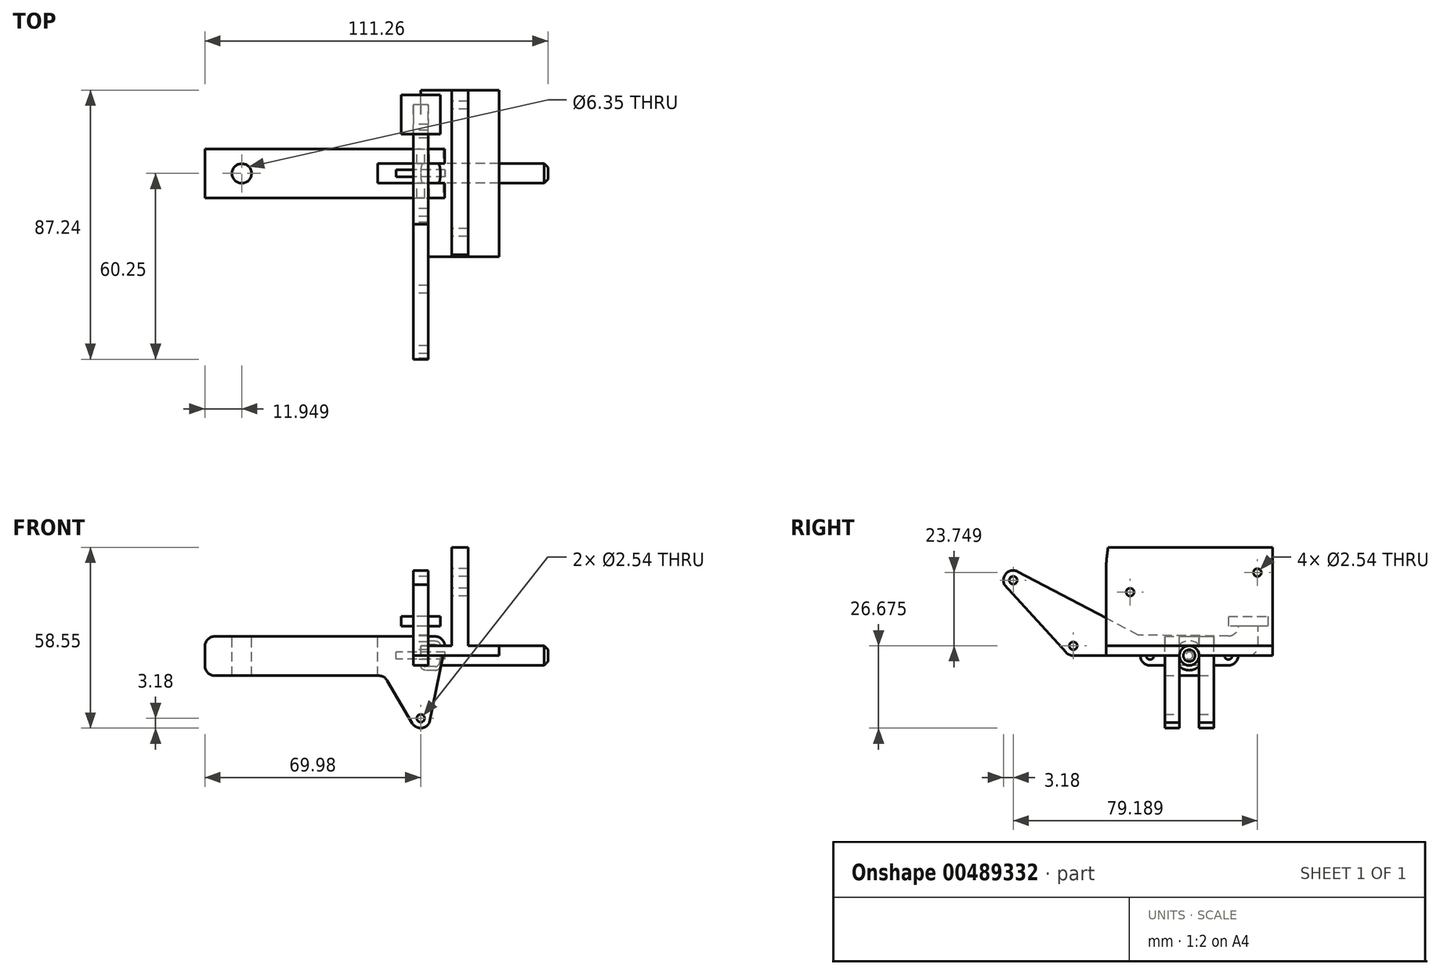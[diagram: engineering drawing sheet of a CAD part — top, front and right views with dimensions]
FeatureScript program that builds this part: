
annotation { "Feature Type Name" : "Feature", "Feature Type Description" : "" }
export const myFeature = defineFeature(function(context is Context, id is Id, definition is map)
    precondition{}
    {
        {
            var Q0;
            Q0=qCreatedBy(makeId("Front.planeOp"),FACE);
            var sketch = newSketch(context, id + "F0", { "sketchPlane" : qUnion([Q0])});
            skCircle(sketch, "E0", {"center": v(0, 0) * mm, "radius": 1.27 * mm});
            skLineSegment(sketch, "E1", {"start": v(-24.73, 6.19) * mm, "end": v(4.64, 6.19) * mm});
            skLineSegment(sketch, "E2", {"start": v(7.75, 2.38) * mm, "end": v(2.83, -21.75) * mm});
            skLineSegment(sketch, "E3", {"start": v(-2.74, -21.93) * mm, "end": v(-10.89, -8.08) * mm});
            skLineSegment(sketch, "E4", {"start": v(-13.62, -6.51) * mm, "end": v(-66.8, -6.51) * mm});
            skLineSegment(sketch, "E5", {"start": v(-69.98, -3.34) * mm, "end": v(-69.98, 3.01) * mm});
            skLineSegment(sketch, "E6", {"start": v(-66.8, 6.19) * mm, "end": v(-24.73, 6.19) * mm});
            skPoint(sketch, "E7.visualSharp", {"position": v(8.53, 6.19) * mm});
            skArc(sketch, "E7.filletArc", {"start": v(7.75, 2.38) * mm, "mid": v(7.1, 5.02) * mm, "end": v(4.64, 6.19) * mm});
            skPoint(sketch, "E8.visualSharp", {"position": v(-11.8, -6.51) * mm});
            skArc(sketch, "E8.filletArc", {"start": v(-10.89, -8.08) * mm, "mid": v(-12.05, -6.93) * mm, "end": v(-13.62, -6.51) * mm});
            skPoint(sketch, "E9.visualSharp", {"position": v(-69.98, 6.19) * mm});
            skArc(sketch, "E9.filletArc", {"start": v(-66.8, 6.19) * mm, "mid": v(-69.05, 5.26) * mm, "end": v(-69.98, 3.01) * mm});
            skPoint(sketch, "E10.visualSharp", {"position": v(-69.98, -6.51) * mm});
            skArc(sketch, "E10.filletArc", {"start": v(-69.98, -3.34) * mm, "mid": v(-69.05, -5.58) * mm, "end": v(-66.8, -6.51) * mm});
            skArc(sketch, "E11", {"start": v(-2.74, -21.93) * mm, "mid": v(0.1, -23.5) * mm, "end": v(2.83, -21.75) * mm});
            skLineSegment(sketch, "E12", {"start": v(0, 0) * mm, "end": v(-69.98, -0.16) * mm, "construction": true});
            skCircle(sketch, "E13", {"center": v(0, -20.32) * mm, "radius": 1.27 * mm});
            skLineSegment(sketch, "E14", {"start": v(0, 0) * mm, "end": v(0, -20.32) * mm, "construction": true});
            skSolve(sketch);
        }
        {
            var Q0;
            Q0 = qSketchRegion(id + "F0", true);
            extrude(context, id + "F1", {"entities" : qUnion([Q0]), "endBound" : BoundingType.SYMMETRIC, "depth" : 15.88 * mm, "offsetDistance" : 25.4 * mm});
        }
        {
            var Q0;
            Q0=makeQuery(id+"F1.opExtrude","SWEPT_FACE",FACE,{"disambiguationData":[OSD([sQuery(id+"F0.wireOp",EDGE,"E1"),sQuery(id+"F0.wireOp",EDGE,"E6")])]});
            var sketch = newSketch(context, id + "F2", { "sketchPlane" : qUnion([Q0])});
            skLineSegment(sketch, "E15.0", {"start": v(7.75, -7.94) * mm, "end": v(7.75, 7.94) * mm});
            skLineSegment(sketch, "E16", {"start": v(7.75, 3.18) * mm, "end": v(-13.88, 3.18) * mm});
            skLineSegment(sketch, "E17", {"start": v(-13.88, 3.18) * mm, "end": v(-13.88, -3.17) * mm});
            skLineSegment(sketch, "E18", {"start": v(-13.88, -3.17) * mm, "end": v(7.75, -3.17) * mm});
            skLineSegment(sketch, "E19", {"start": v(7.75, 0) * mm, "end": v(-66.8, 0) * mm, "construction": true});
            skCircle(sketch, "E20", {"center": v(-58.03, 0) * mm, "radius": 3.18 * mm});
            skLineSegment(sketch, "E21.0", {"start": v(-66.8, 7.94) * mm, "end": v(4.64, 7.94) * mm});
            skLineSegment(sketch, "E22.0", {"start": v(-66.8, -7.94) * mm, "end": v(4.64, -7.94) * mm});
            skSolve(sketch);
        }
        {
            var Q0;
            Q0 = qSketchRegion(id + "F2", true);
            extrude(context, id + "F3", {"entities" : qUnion([Q0]), "operationType" : NewBodyOperationType.REMOVE, "endBound" : BoundingType.THROUGH_ALL, "oppositeDirection" : true, "depth" : 25.4 * mm, "offsetDistance" : 25.4 * mm});
        }
        {
            var Q0;
            {var subQ2=sQuery(id+"F0.wireOp",EDGE,"E2");Q0=makeQuery(id+"F3.boolean.opBoolean","SPLIT",FACE,{"disambiguationData":[TD([makeQuery(id+"F3.opExtrude","SWEPT_FACE",FACE,{"disambiguationData":[OSD([sQuery(id+"F2.wireOp",EDGE,"E16")])]})])],"derivedFrom":makeQuery(id+"F1.opExtrude","SWEPT_FACE",FACE,{"disambiguationData":[OSD([subQ2])]})});}
            var sketch = newSketch(context, id + "F4", { "sketchPlane" : qUnion([Q0])});
            skLineSegment(sketch, "E23.0", {"start": v(-3.17, 3.88) * mm, "end": v(3.18, 3.88) * mm});
            skLineSegment(sketch, "E24.0", {"start": v(3.18, 5.12) * mm, "end": v(-3.17, 5.12) * mm});
            skLineSegment(sketch, "E25", {"start": v(3.18, 5.12) * mm, "end": v(3.18, 3.88) * mm});
            skLineSegment(sketch, "E26", {"start": v(-3.17, 5.12) * mm, "end": v(-3.17, 3.88) * mm});
            skSolve(sketch);
        }
        {
            var Q0;
            Q0 = qSketchRegion(id + "F4", true);
            extrude(context, id + "F5", {"entities" : qUnion([Q0]), "operationType" : NewBodyOperationType.REMOVE, "oppositeDirection" : true, "depth" : 7.85 * mm, "offsetDistance" : 25.4 * mm});
        }
        {
            var Q0;
            Q0=qCreatedBy(makeId("Front.planeOp"),FACE);
            var sketch = newSketch(context, id + "F6", { "sketchPlane" : qUnion([Q0])});
            skLineSegment(sketch, "E27", {"start": v(0, 0) * mm, "end": v(25.4, 0) * mm});
            skLineSegment(sketch, "E28", {"start": v(0, 0) * mm, "end": v(0, 3.18) * mm});
            skLineSegment(sketch, "E29", {"start": v(0, 3.18) * mm, "end": v(15.36, 3.18) * mm});
            skLineSegment(sketch, "E30", {"start": v(25.4, 0) * mm, "end": v(25.4, 3.18) * mm});
            skLineSegment(sketch, "E31", {"start": v(25.4, 3.18) * mm, "end": v(10.04, 3.18) * mm});
            skLineSegment(sketch, "E32", {"start": v(15.36, 3.18) * mm, "end": v(15.36, 35.05) * mm});
            skLineSegment(sketch, "E33", {"start": v(10.04, 35.05) * mm, "end": v(15.36, 35.05) * mm});
            skLineSegment(sketch, "E34", {"start": v(10.04, 35.05) * mm, "end": v(10.04, 3.18) * mm});
            skSolve(sketch);
        }
        {
            var Q0;
            Q0 = qSketchRegion(id + "F6", true);
            extrude(context, id + "F7", {"entities" : qUnion([Q0]), "endBound" : BoundingType.SYMMETRIC, "depth" : 53.97 * mm, "offsetDistance" : 25.4 * mm});
        }
        {
            var Q0;
            Q0=makeQuery(id+"F7.opExtrude","SWEPT_FACE",FACE,{"disambiguationData":[OSD([sQuery(id+"F6.wireOp",EDGE,"E34")])]});
            var sketch = newSketch(context, id + "F8", { "sketchPlane" : qUnion([Q0])});
            skLineSegment(sketch, "E35.0.0", {"start": v(-26.99, 13.43) * mm, "end": v(-26.99, 3.18) * mm});
            skLineSegment(sketch, "E35.0.2", {"start": v(26.99, 3.18) * mm, "end": v(26.99, 26.92) * mm});
            skLineSegment(sketch, "E35.0.3", {"start": v(-26.99, 3.18) * mm, "end": v(26.99, 3.18) * mm});
            skPoint(sketch, "E36.visualSharp", {"position": v(26.99, 35.05) * mm});
            skLineSegment(sketch, "E37.0.0", {"start": v(-26.99, 0) * mm, "end": v(-26.99, 3.17) * mm});
            skLineSegment(sketch, "E37.0.1", {"start": v(-26.99, 3.17) * mm, "end": v(26.99, 3.17) * mm});
            skLineSegment(sketch, "E37.0.2", {"start": v(26.99, 3.17) * mm, "end": v(26.99, 0) * mm});
            skLineSegment(sketch, "E37.0.3", {"start": v(26.99, 0) * mm, "end": v(-26.99, 0) * mm});
            skArc(sketch, "E38", {"start": v(-71.23, 26.92) * mm, "mid": v(-22.12, 76.03) * mm, "end": v(26.99, 26.92) * mm});
            skCircle(sketch, "E39", {"center": v(-22.12, 26.92) * mm, "radius": 1.27 * mm});
            skLineSegment(sketch, "E40", {"start": v(-65.76, 17.46) * mm, "end": v(-71.23, 26.92) * mm});
            skLineSegment(sketch, "E41", {"start": v(-68.51, 12.7) * mm, "end": v(9.87, 12.7) * mm});
            skPoint(sketch, "E42.visualSharp", {"position": v(-63.01, 12.7) * mm});
            skArc(sketch, "E42.filletArc", {"start": v(-65.76, 17.46) * mm, "mid": v(-71.26, 17.46) * mm, "end": v(-68.51, 12.7) * mm});
            skPoint(sketch, "E43.visualSharp", {"position": v(12.82, 12.7) * mm});
            skArc(sketch, "E43.filletArc", {"start": v(9.87, 12.7) * mm, "mid": v(12.03, 13.55) * mm, "end": v(13.04, 15.65) * mm});
            skCircle(sketch, "E44", {"center": v(19.16, 20.57) * mm, "radius": 1.27 * mm});
            skLineSegment(sketch, "E45", {"start": v(13.04, 15.65) * mm, "end": v(15.32, 26.92) * mm});
            skLineSegment(sketch, "E46", {"start": v(15.32, 26.92) * mm, "end": v(22.7, 26.67) * mm});
            skLineSegment(sketch, "E47", {"start": v(22.7, 26.67) * mm, "end": v(-26.99, 13.43) * mm});
            skPoint(sketch, "E48.orphan", {"position": v(-26.99, 35.05) * mm});
            skSolve(sketch);
        }
        {
            var Q0;
            {var subQ4=sQuery(id+"F8.wireOp",EDGE,"E38");Q0=makeQuery(id+"F8.imprint","IMPRINT",FACE,{"disambiguationData":[TD([[makeQuery(id+"F8.imprint","IMPRINT",EDGE,{"derivedFrom":subQ4}),-1.0]])]});}
            var Q1;
            Q1=makeQuery(id+"F8.imprint","IMPRINT",FACE,{"disambiguationData":[TD([[makeQuery(id+"F8.imprint","IMPRINT",EDGE,{"derivedFrom":sQuery(id+"F8.wireOp",EDGE,"E39")}),1.0]])]});
            var Q2;
            Q2=makeQuery(id+"F8.imprint","IMPRINT",FACE,{"disambiguationData":[TD([[makeQuery(id+"F8.imprint","IMPRINT",EDGE,{"derivedFrom":sQuery(id+"F8.wireOp",EDGE,"E44")}),1.0]])]});
            extrude(context, id + "F9", {"entities" : qUnion([Q0, Q1, Q2]), "operationType" : NewBodyOperationType.REMOVE, "endBound" : BoundingType.THROUGH_ALL, "oppositeDirection" : true, "depth" : 25.4 * mm, "offsetDistance" : 25.4 * mm});
        }
        {
            var Q0;
            Q0=qCreatedBy(makeId("Right.planeOp"),FACE);
            var sketch = newSketch(context, id + "F10", { "sketchPlane" : qUnion([Q0])});
            skLineSegment(sketch, "E49", {"start": v(0, 0) * mm, "end": v(19.13, 0) * mm});
            skLineSegment(sketch, "E50", {"start": v(22.3, 3.18) * mm, "end": v(22.3, 6.35) * mm});
            skLineSegment(sketch, "E51", {"start": v(12.75, 6.38) * mm, "end": v(0, 6.49) * mm});
            skLineSegment(sketch, "E52", {"start": v(27.19, 9.52) * mm, "end": v(27.19, 0) * mm, "construction": true});
            skLineSegment(sketch, "E53", {"start": v(22.3, 3.17) * mm, "end": v(0, 3.17) * mm, "construction": true});
            skLineSegment(sketch, "E54", {"start": v(15.95, 9.55) * mm, "end": v(15.95, 9.55) * mm});
            skLineSegment(sketch, "E55", {"start": v(22.3, 6.35) * mm, "end": v(22.3, 9.55) * mm});
            skLineSegment(sketch, "E56", {"start": v(22.3, 9.55) * mm, "end": v(15.95, 9.55) * mm});
            skLineSegment(sketch, "E57", {"start": v(15.95, 9.55) * mm, "end": v(12.78, 9.55) * mm});
            skLineSegment(sketch, "E58", {"start": v(12.78, 9.55) * mm, "end": v(12.78, 12.73) * mm});
            skLineSegment(sketch, "E59", {"start": v(12.78, 12.73) * mm, "end": v(25.48, 12.73) * mm});
            skLineSegment(sketch, "E60", {"start": v(25.48, 12.73) * mm, "end": v(25.48, 9.55) * mm});
            skLineSegment(sketch, "E61", {"start": v(25.48, 9.55) * mm, "end": v(22.3, 9.55) * mm});
            skPoint(sketch, "E62.visualSharp", {"position": v(22.3, 0) * mm});
            skArc(sketch, "E62.filletArc", {"start": v(19.13, 0) * mm, "mid": v(21.37, 0.93) * mm, "end": v(22.3, 3.18) * mm});
            skPoint(sketch, "E63.visualSharp", {"position": v(15.95, 6.35) * mm});
            skArc(sketch, "E63.filletArc", {"start": v(12.75, 6.38) * mm, "mid": v(15.02, 7.3) * mm, "end": v(15.95, 9.55) * mm});
            skLineSegment(sketch, "E64", {"start": v(0, 6.49) * mm, "end": v(-16.47, 6.63) * mm});
            skLineSegment(sketch, "E65", {"start": v(-16.47, 6.63) * mm, "end": v(-55.6, 27.23) * mm});
            skLineSegment(sketch, "E66", {"start": v(0, 0) * mm, "end": v(-37.6, 0) * mm});
            skLineSegment(sketch, "E67", {"start": v(-39.95, 1.04) * mm, "end": v(-59.93, 23.04) * mm});
            skArc(sketch, "E68", {"start": v(-55.6, 27.23) * mm, "mid": v(-59.27, 26.7) * mm, "end": v(-59.93, 23.04) * mm});
            skPoint(sketch, "E69.visualSharp", {"position": v(-39, 0) * mm});
            skArc(sketch, "E69.filletArc", {"start": v(-39.95, 1.04) * mm, "mid": v(-38.89, 0.27) * mm, "end": v(-37.6, 0) * mm});
            skLineSegment(sketch, "E70", {"start": v(-57.07, 24.42) * mm, "end": v(-37.6, 3.17) * mm, "construction": true});
            skLineSegment(sketch, "E71", {"start": v(-37.6, 3.17) * mm, "end": v(0, 3.17) * mm, "construction": true});
            skCircle(sketch, "E72", {"center": v(-37.6, 3.17) * mm, "radius": 1.27 * mm});
            skCircle(sketch, "E73", {"center": v(-57.07, 24.42) * mm, "radius": 1.27 * mm});
            skLineSegment(sketch, "E74", {"start": v(19.13, 9.55) * mm, "end": v(19.13, 0) * mm, "construction": true});
            skSolve(sketch);
        }
        {
            var Q0;
            Q0=makeQuery(id+"F10.imprint","IMPRINT",FACE,{"disambiguationData":[TD([[makeQuery(id+"F10.imprint","IMPRINT",EDGE,{"derivedFrom":sQuery(id+"F10.wireOp",EDGE,"E49")}),1.0]])]});
            extrude(context, id + "F11", {"entities" : qUnion([Q0]), "endBound" : BoundingType.SYMMETRIC, "depth" : 4.78 * mm, "offsetDistance" : 25.4 * mm});
        }
        {
            var Q0;
            Q0=makeQuery(id+"F10.imprint","IMPRINT",FACE,{"disambiguationData":[TD([[makeQuery(id+"F10.imprint","IMPRINT",EDGE,{"derivedFrom":sQuery(id+"F10.wireOp",EDGE,"E56")}),-1.0]])]});
            extrude(context, id + "F12", {"entities" : qUnion([Q0]), "operationType" : NewBodyOperationType.ADD, "endBound" : BoundingType.SYMMETRIC, "depth" : 12.7 * mm, "offsetDistance" : 25.4 * mm});
        }
        {
            var Q0;
            Q0=qCreatedBy(makeId("Right.planeOp"),FACE);
            var sketch = newSketch(context, id + "F13", { "sketchPlane" : qUnion([Q0])});
            skLineSegment(sketch, "E75.bottom", {"start": v(12.7, 3.17) * mm, "end": v(-12.7, 3.17) * mm});
            skLineSegment(sketch, "E75.top", {"start": v(12.7, -3.18) * mm, "end": v(-12.7, -3.18) * mm});
            skLineSegment(sketch, "E75.left", {"start": v(12.7, 3.17) * mm, "end": v(12.7, -3.18) * mm, "construction": true});
            skLineSegment(sketch, "E75.right", {"start": v(-12.7, 3.17) * mm, "end": v(-12.7, -3.18) * mm, "construction": true});
            skPoint(sketch, "E75.middle", {"position": v(0, 0) * mm});
            skArc(sketch, "E76", {"start": v(12.7, -3.18) * mm, "mid": v(15.88, 0) * mm, "end": v(12.7, 3.17) * mm});
            skArc(sketch, "E77", {"start": v(-12.7, 3.17) * mm, "mid": v(-15.88, 0) * mm, "end": v(-12.7, -3.18) * mm});
            skCircle(sketch, "E78", {"center": v(-12.7, 0) * mm, "radius": 1.27 * mm});
            skCircle(sketch, "E79", {"center": v(12.7, 0) * mm, "radius": 1.27 * mm});
            skSolve(sketch);
        }
        {
            var Q0;
            Q0 = qSketchRegion(id + "F13", true);
            extrude(context, id + "F14", {"entities" : qUnion([Q0]), "endBound" : BoundingType.SYMMETRIC, "depth" : 4.78 * mm, "offsetDistance" : 25.4 * mm});
        }
        {
            var Q0;
            Q0=qCreatedBy(makeId("Right.planeOp"),FACE);
            var sketch = newSketch(context, id + "F15", { "sketchPlane" : qUnion([Q0])});
            skCircle(sketch, "E80", {"center": v(0, 0) * mm, "radius": 1.14 * mm});
            skSolve(sketch);
        }
        {
            var Q0;
            Q0 = qSketchRegion(id + "F15", true);
            extrude(context, id + "F16", {"entities" : qUnion([Q0]), "endBound" : BoundingType.SYMMETRIC, "depth" : 15.88 * mm, "offsetDistance" : 25.4 * mm});
        }
        {
            var Q0;
            Q0=qCreatedBy(makeId("Right.planeOp"),FACE);
            var sketch = newSketch(context, id + "F17", { "sketchPlane" : qUnion([Q0])});
            skCircle(sketch, "E81", {"center": v(0, 0) * mm, "radius": 4.76 * mm});
            skCircle(sketch, "E82", {"center": v(0, 0) * mm, "radius": 3.18 * mm});
            skSolve(sketch);
        }
        {
            var Q0;
            Q0=makeQuery(id+"F17.imprint","IMPRINT",FACE,{"disambiguationData":[TD([[makeQuery(id+"F17.imprint","IMPRINT",EDGE,{"derivedFrom":sQuery(id+"F17.wireOp",EDGE,"E82")}),1.0]])]});
            extrude(context, id + "F18", {"entities" : qUnion([Q0]), "depth" : 41.27 * mm, "offsetDistance" : 25.4 * mm});
        }
        {
            var Q0;
            Q0=makeQuery(id+"F17.imprint","IMPRINT",FACE,{"disambiguationData":[TD([[makeQuery(id+"F17.imprint","IMPRINT",EDGE,{"derivedFrom":sQuery(id+"F17.wireOp",EDGE,"E81")}),1.0]])]});
            extrude(context, id + "F19", {"entities" : qUnion([Q0]), "operationType" : NewBodyOperationType.ADD, "depth" : 6.35 * mm, "offsetDistance" : 25.4 * mm});
        }
        {
            var Q0;
            Q0=makeQuery(id+"F19.opExtrude","CAP_EDGE",EDGE,{"disambiguationData":[OSD([sQuery(id+"F17.wireOp",EDGE,"E81")])],"isStart":false});
            var Q1;
            Q1=makeQuery(id+"F19.opExtrude","CAP_EDGE",EDGE,{"disambiguationData":[OSD([sQuery(id+"F17.wireOp",EDGE,"E81")])],"isStart":true});
            fillet(context, id + "F20", {"entities" : qUnion([Q0, Q1]), "radius" : 1.59 * mm, "tangentPropagation" : true, "allowEdgeOverflow" : false});
        }
        {
            var Q0;
            Q0=makeQuery(id+"F18.opExtrude","CAP_EDGE",EDGE,{"disambiguationData":[OSD([sQuery(id+"F17.wireOp",EDGE,"E82")])],"isStart":false});
            chamfer(context, id + "F21", {"entities" : qUnion([Q0]), "width" : 1.27 * mm, "tangentPropagation" : true});
        }
    });
